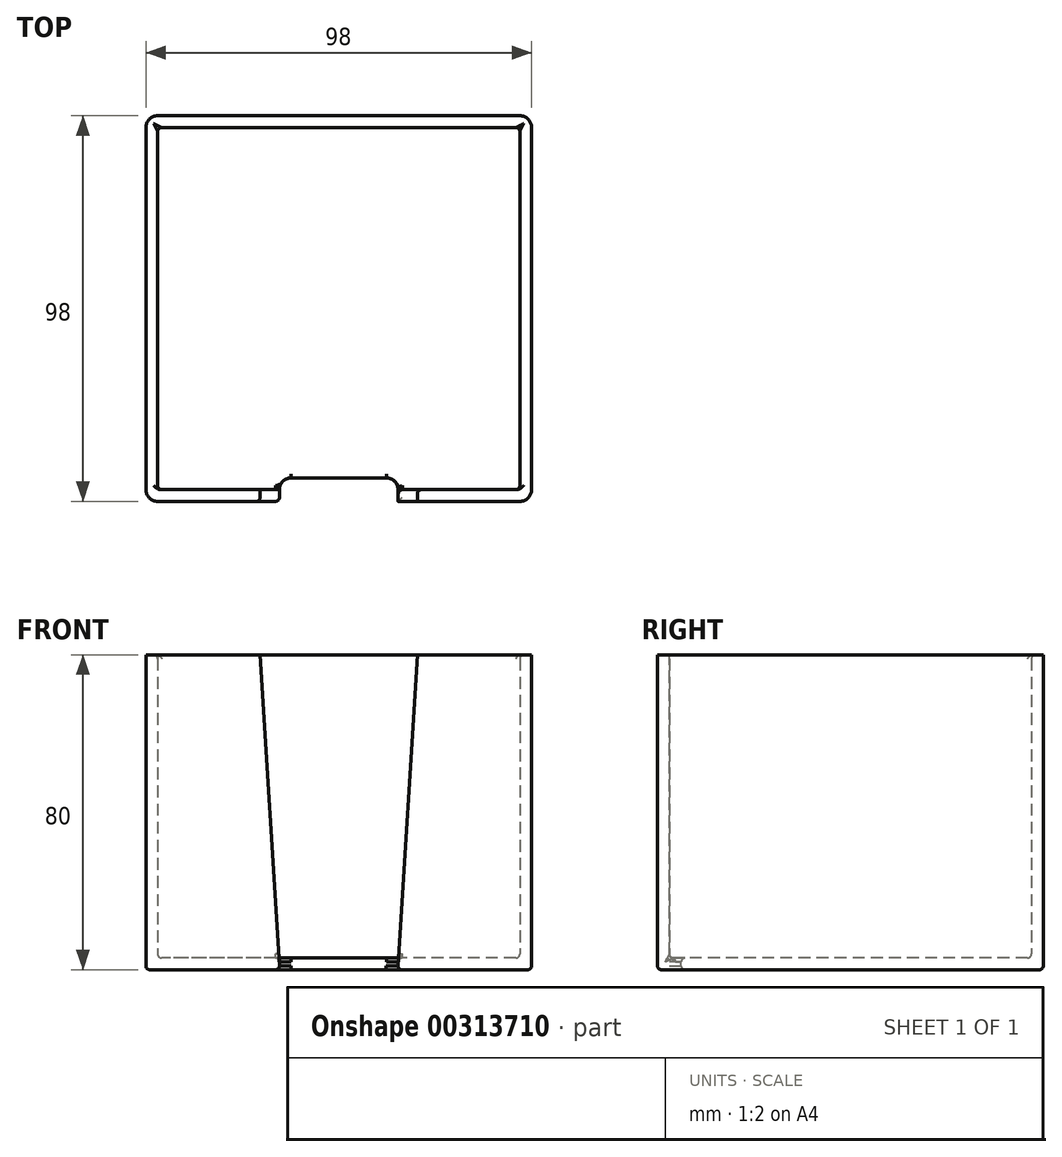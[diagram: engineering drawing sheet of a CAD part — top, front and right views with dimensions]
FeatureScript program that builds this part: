
annotation { "Feature Type Name" : "Feature", "Feature Type Description" : "" }
export const myFeature = defineFeature(function(context is Context, id is Id, definition is map)
    precondition{}
    {
        {
            var Q0;
            Q0=qCreatedBy(makeId("Top.planeOp"),FACE);
            var sketch = newSketch(context, id + "F0", { "sketchPlane" : qUnion([Q0])});
            skLineSegment(sketch, "E0.bottom", {"start": v(49, 49) * mm, "end": v(-49, 49) * mm});
            skLineSegment(sketch, "E0.top", {"start": v(49, -49) * mm, "end": v(-49, -49) * mm});
            skLineSegment(sketch, "E0.left", {"start": v(49, 49) * mm, "end": v(49, -49) * mm});
            skLineSegment(sketch, "E0.right", {"start": v(-49, 49) * mm, "end": v(-49, -49) * mm});
            skPoint(sketch, "E0.middle", {"position": v(0, 0) * mm});
            skSolve(sketch);
        }
        {
            var Q0;
            Q0 = qSketchRegion(id + "F0", true);
            extrude(context, id + "F1", {"entities" : qUnion([Q0]), "depth" : 80 * mm});
        }
        {
            var Q0;
            Q0=makeQuery(id+"F1.opExtrude","CAP_FACE",FACE,{"disambiguationData":[OSD([sQuery(id+"F0.wireOp",EDGE,"E0.bottom"),sQuery(id+"F0.wireOp",EDGE,"E0.top"),sQuery(id+"F0.wireOp",EDGE,"E0.left"),sQuery(id+"F0.wireOp",EDGE,"E0.right")])],"isStart":false});
            shell(context, id + "F2", {"entities" : qUnion([Q0]), "thickness" : 3 * mm});
        }
        {
            var Q0;
            Q0=makeQuery(id+"F1.opExtrude","SWEPT_FACE",FACE,{"disambiguationData":[OSD([sQuery(id+"F0.wireOp",EDGE,"E0.top")])]});
            var sketch = newSketch(context, id + "F3", { "sketchPlane" : qUnion([Q0])});
            skLineSegment(sketch, "E1", {"start": v(15, 0) * mm, "end": v(20, 80) * mm});
            skLineSegment(sketch, "E2.MirrorCS", {"start": v(-15, 0) * mm, "end": v(-20, 80) * mm});
            skLineSegment(sketch, "E3", {"start": v(-15, 0) * mm, "end": v(15, 0) * mm});
            skLineSegment(sketch, "E4", {"start": v(-20, 80) * mm, "end": v(20, 80) * mm});
            skSolve(sketch);
        }
        {
            var Q0;
            Q0=makeQuery(id+"F3.imprint","IMPRINT",FACE,{"disambiguationData":[TD([[makeQuery(id+"F3.imprint","IMPRINT",EDGE,{"derivedFrom":sQuery(id+"F3.wireOp",EDGE,"E1")}),1.0]])]});
            extrude(context, id + "F4", {"entities" : qUnion([Q0]), "operationType" : NewBodyOperationType.REMOVE, "oppositeDirection" : true, "depth" : 6 * mm});
        }
        {
            var Q0;
            Q0=makeQuery(id+"F1.opExtrude","SWEPT_EDGE",EDGE,{"disambiguationData":[OSD([sQuery(id+"F0.wireOp",EDGE,"E0.top"),sQuery(id+"F0.wireOp",EDGE,"E0.left")])]});
            var Q1;
            Q1=makeQuery(id+"F1.opExtrude","SWEPT_EDGE",EDGE,{"disambiguationData":[OSD([sQuery(id+"F0.wireOp",EDGE,"E0.top"),sQuery(id+"F0.wireOp",EDGE,"E0.right")])]});
            var Q2;
            Q2=makeQuery(id+"F1.opExtrude","SWEPT_EDGE",EDGE,{"disambiguationData":[OSD([sQuery(id+"F0.wireOp",EDGE,"E0.bottom"),sQuery(id+"F0.wireOp",EDGE,"E0.right")])]});
            var Q3;
            Q3=makeQuery(id+"F1.opExtrude","SWEPT_EDGE",EDGE,{"disambiguationData":[OSD([sQuery(id+"F0.wireOp",EDGE,"E0.bottom"),sQuery(id+"F0.wireOp",EDGE,"E0.left")])]});
            var Q4;
            Q4=makeQuery(id+"F4.boolean.opBoolean","COPY",EDGE,{"derivedFrom":makeQuery(id+"F4.opExtrude","CAP_EDGE",EDGE,{"disambiguationData":[OSD([sQuery(id+"F3.wireOp",EDGE,"E1")])],"isStart":false})});
            var Q5;
            Q5=makeQuery(id+"F4.boolean.opBoolean","COPY",EDGE,{"derivedFrom":makeQuery(id+"F4.opExtrude","CAP_EDGE",EDGE,{"disambiguationData":[OSD([sQuery(id+"F3.wireOp",EDGE,"E2.MirrorCS")])],"isStart":false})});
            var Q6;
            Q6=makeQuery(id+"F4.boolean.opBoolean","COPY",EDGE,{"derivedFrom":makeQuery(id+"F4.opExtrude","SWEPT_EDGE",EDGE,{"disambiguationData":[OSD([sQuery(id+"F0.wireOp",EDGE,"E0.top"),sQuery(id+"F3.wireOp",EDGE,"E2.MirrorCS"),sQuery(id+"F3.wireOp",EDGE,"E4")])]})});
            var Q7;
            Q7=makeQuery(id+"F4.boolean.opBoolean","COPY",EDGE,{"derivedFrom":makeQuery(id+"F4.opExtrude","SWEPT_EDGE",EDGE,{"disambiguationData":[OSD([sQuery(id+"F0.wireOp",EDGE,"E0.top"),sQuery(id+"F3.wireOp",EDGE,"E1"),sQuery(id+"F3.wireOp",EDGE,"E4")])]})});
            fillet(context, id + "F5", {"entities" : qUnion([Q0, Q1, Q2, Q3, Q4, Q5, Q6, Q7]), "radius" : 3 * mm, "tangentPropagation" : true, "allowEdgeOverflow" : false});
        }
        {
            var Q0;
            Q0=makeQuery(id+"F5.opFillet","BLEND_EDGE",EDGE,{"blendedFrom":[makeQuery(id+"F4.boolean.opBoolean","COPY",EDGE,{"derivedFrom":makeQuery(id+"F4.opExtrude","CAP_EDGE",EDGE,{"disambiguationData":[OSD([sQuery(id+"F3.wireOp",EDGE,"E2.MirrorCS")])],"isStart":false})}),makeQuery(id+"F2.opShell","OFFSET_FACE",FACE,{"disambiguationData":[OSD([sQuery(id+"F0.wireOp",EDGE,"E0.bottom"),sQuery(id+"F0.wireOp",EDGE,"E0.top"),sQuery(id+"F0.wireOp",EDGE,"E0.left"),sQuery(id+"F0.wireOp",EDGE,"E0.right")])]})],"blendedInto":[makeQuery(id+"F2.opShell","OFFSET_FACE",FACE,{"disambiguationData":[OSD([sQuery(id+"F0.wireOp",EDGE,"E0.bottom"),sQuery(id+"F0.wireOp",EDGE,"E0.top"),sQuery(id+"F0.wireOp",EDGE,"E0.left"),sQuery(id+"F0.wireOp",EDGE,"E0.right")])]})]});
            var Q1;
            Q1=makeQuery(id+"F4.boolean.opBoolean","INTERSECT",EDGE,{"derivedFrom":[makeQuery(id+"F2.opShell","OFFSET_FACE",FACE,{"disambiguationData":[OSD([sQuery(id+"F0.wireOp",EDGE,"E0.bottom"),sQuery(id+"F0.wireOp",EDGE,"E0.top"),sQuery(id+"F0.wireOp",EDGE,"E0.left"),sQuery(id+"F0.wireOp",EDGE,"E0.right")])]}),makeQuery(id+"F4.opExtrude","CAP_FACE",FACE,{"disambiguationData":[OSD([sQuery(id+"F3.wireOp",EDGE,"E1"),sQuery(id+"F3.wireOp",EDGE,"E2.MirrorCS"),sQuery(id+"F3.wireOp",EDGE,"E3"),sQuery(id+"F3.wireOp",EDGE,"E4")])],"isStart":false})]});
            var Q2;
            Q2=makeQuery(id+"F5.opFillet","BLEND_EDGE",EDGE,{"blendedFrom":[makeQuery(id+"F4.boolean.opBoolean","COPY",EDGE,{"derivedFrom":makeQuery(id+"F4.opExtrude","CAP_EDGE",EDGE,{"disambiguationData":[OSD([sQuery(id+"F3.wireOp",EDGE,"E1")])],"isStart":false})}),makeQuery(id+"F2.opShell","OFFSET_FACE",FACE,{"disambiguationData":[OSD([sQuery(id+"F0.wireOp",EDGE,"E0.bottom"),sQuery(id+"F0.wireOp",EDGE,"E0.top"),sQuery(id+"F0.wireOp",EDGE,"E0.left"),sQuery(id+"F0.wireOp",EDGE,"E0.right")])]})],"blendedInto":[makeQuery(id+"F2.opShell","OFFSET_FACE",FACE,{"disambiguationData":[OSD([sQuery(id+"F0.wireOp",EDGE,"E0.bottom"),sQuery(id+"F0.wireOp",EDGE,"E0.top"),sQuery(id+"F0.wireOp",EDGE,"E0.left"),sQuery(id+"F0.wireOp",EDGE,"E0.right")])]})]});
            var Q3;
            Q3=makeQuery(id+"F4.boolean.opBoolean","INTERSECT",EDGE,{"derivedFrom":[makeQuery(id+"F2.opShell","OFFSET_FACE",FACE,{"disambiguationData":[OSD([sQuery(id+"F0.wireOp",EDGE,"E0.top")])]}),makeQuery(id+"F4.opExtrude","SWEPT_FACE",FACE,{"disambiguationData":[OSD([sQuery(id+"F3.wireOp",EDGE,"E1")])]})]});
            var Q4;
            {var subQ0=sQuery(id+"F0.wireOp",EDGE,"E0.left");Q4=makeQuery(id+"F2.opShell","OFFSET_EDGE",EDGE,{"disambiguationData":[OSD([subQ0]),TDD([makeQuery(id+"F1.opExtrude","CAP_EDGE",EDGE,{"disambiguationData":[OSD([subQ0])],"isStart":false})])]});}
            var Q5;
            {var subQ0=sQuery(id+"F0.wireOp",EDGE,"E0.right");var subQ2=sQuery(id+"F0.wireOp",EDGE,"E0.top");var subQ4=sQuery(id+"F3.wireOp",EDGE,"E2.MirrorCS");Q5=makeQuery(id+"F5.opFillet","BLEND_EDGE",EDGE,{"blendedFrom":[makeQuery(id+"F4.boolean.opBoolean","COPY",EDGE,{"derivedFrom":makeQuery(id+"F4.opExtrude","SWEPT_EDGE",EDGE,{"disambiguationData":[OSD([subQ2,subQ4,sQuery(id+"F3.wireOp",EDGE,"E4")])]})}),makeQuery(id+"F4.boolean.opBoolean","SPLIT",FACE,{"disambiguationData":[TD([makeQuery(id+"F2.opShell","OFFSET_FACE",FACE,{"disambiguationData":[OSD([subQ0])]})])],"derivedFrom":makeQuery(id+"F2.opShell","OFFSET_FACE",FACE,{"disambiguationData":[OSD([subQ2])]})})],"blendedInto":[makeQuery(id+"F4.boolean.opBoolean","SPLIT",FACE,{"disambiguationData":[TD([makeQuery(id+"F2.opShell","OFFSET_FACE",FACE,{"disambiguationData":[OSD([subQ0])]})])],"derivedFrom":makeQuery(id+"F2.opShell","OFFSET_FACE",FACE,{"disambiguationData":[OSD([subQ2])]})})]});}
            var Q6;
            {var subQ0=sQuery(id+"F0.wireOp",EDGE,"E0.right");Q6=makeQuery(id+"F2.opShell","OFFSET_EDGE",EDGE,{"disambiguationData":[OSD([subQ0]),TDD([makeQuery(id+"F1.opExtrude","CAP_EDGE",EDGE,{"disambiguationData":[OSD([subQ0])],"isStart":false})])]});}
            var Q7;
            {var subQ0=sQuery(id+"F0.wireOp",EDGE,"E0.bottom");Q7=makeQuery(id+"F2.opShell","OFFSET_EDGE",EDGE,{"disambiguationData":[OSD([subQ0]),TDD([makeQuery(id+"F1.opExtrude","CAP_EDGE",EDGE,{"disambiguationData":[OSD([subQ0])],"isStart":false})])]});}
            var Q8;
            Q8=makeQuery(id+"F4.boolean.opBoolean","COPY",EDGE,{"derivedFrom":makeQuery(id+"F4.opExtrude","CAP_EDGE",EDGE,{"disambiguationData":[OSD([sQuery(id+"F3.wireOp",EDGE,"E2.MirrorCS")])],"isStart":true})});
            var Q9;
            {var subQ0=sQuery(id+"F0.wireOp",EDGE,"E0.right");var subQ2=sQuery(id+"F0.wireOp",EDGE,"E0.top");var subQ4=sQuery(id+"F3.wireOp",EDGE,"E2.MirrorCS");Q9=makeQuery(id+"F5.opFillet","BLEND_EDGE",EDGE,{"blendedFrom":[makeQuery(id+"F4.boolean.opBoolean","COPY",EDGE,{"derivedFrom":makeQuery(id+"F4.opExtrude","SWEPT_EDGE",EDGE,{"disambiguationData":[OSD([subQ2,subQ4,sQuery(id+"F3.wireOp",EDGE,"E4")])]})}),makeQuery(id+"F4.boolean.opBoolean","SPLIT",FACE,{"disambiguationData":[TD([makeQuery(id+"F1.opExtrude","SWEPT_FACE",FACE,{"disambiguationData":[OSD([subQ0])]})])],"derivedFrom":makeQuery(id+"F1.opExtrude","SWEPT_FACE",FACE,{"disambiguationData":[OSD([subQ2])]})})],"blendedInto":[makeQuery(id+"F4.boolean.opBoolean","SPLIT",FACE,{"disambiguationData":[TD([makeQuery(id+"F1.opExtrude","SWEPT_FACE",FACE,{"disambiguationData":[OSD([subQ0])]})])],"derivedFrom":makeQuery(id+"F1.opExtrude","SWEPT_FACE",FACE,{"disambiguationData":[OSD([subQ2])]})})]});}
            var Q10;
            Q10=makeQuery(id+"F1.opExtrude","CAP_FACE",FACE,{"disambiguationData":[OSD([sQuery(id+"F0.wireOp",EDGE,"E0.bottom"),sQuery(id+"F0.wireOp",EDGE,"E0.top"),sQuery(id+"F0.wireOp",EDGE,"E0.left"),sQuery(id+"F0.wireOp",EDGE,"E0.right")])],"isStart":true});
            fillet(context, id + "F6", {"entities" : qUnion([Q0, Q1, Q2, Q3, Q4, Q5, Q6, Q7, Q8, Q9, Q10]), "radius" : 1 * mm, "tangentPropagation" : true, "allowEdgeOverflow" : false});
        }
        {
            var Q0;
            Q0=makeQuery(id+"F2.opShell","OFFSET_EDGE",EDGE,{"disambiguationData":[OSD([sQuery(id+"F0.wireOp",EDGE,"E0.bottom"),sQuery(id+"F0.wireOp",EDGE,"E0.left")])]});
            var Q1;
            Q1=makeQuery(id+"F2.opShell","OFFSET_EDGE",EDGE,{"disambiguationData":[OSD([sQuery(id+"F0.wireOp",EDGE,"E0.top"),sQuery(id+"F0.wireOp",EDGE,"E0.left")])]});
            var Q2;
            Q2=makeQuery(id+"F2.opShell","OFFSET_EDGE",EDGE,{"disambiguationData":[OSD([sQuery(id+"F0.wireOp",EDGE,"E0.top"),sQuery(id+"F0.wireOp",EDGE,"E0.right")])]});
            var Q3;
            Q3=makeQuery(id+"F2.opShell","OFFSET_EDGE",EDGE,{"disambiguationData":[OSD([sQuery(id+"F0.wireOp",EDGE,"E0.bottom"),sQuery(id+"F0.wireOp",EDGE,"E0.right")])]});
            var Q4;
            {var subQ0=sQuery(id+"F0.wireOp",EDGE,"E0.left");Q4=makeQuery(id+"F2.opShell","OFFSET_EDGE",EDGE,{"disambiguationData":[OSD([subQ0]),TDD([makeQuery(id+"F1.opExtrude","CAP_EDGE",EDGE,{"disambiguationData":[OSD([subQ0])],"isStart":true})])]});}
            var Q5;
            Q5=makeQuery(id+"F2.opShell","OFFSET_FACE",FACE,{"disambiguationData":[OSD([sQuery(id+"F0.wireOp",EDGE,"E0.bottom"),sQuery(id+"F0.wireOp",EDGE,"E0.top"),sQuery(id+"F0.wireOp",EDGE,"E0.left"),sQuery(id+"F0.wireOp",EDGE,"E0.right")])]});
            fillet(context, id + "F7", {"entities" : qUnion([Q0, Q1, Q2, Q3, Q4, Q5]), "radius" : 1 * mm, "tangentPropagation" : true, "allowEdgeOverflow" : false});
        }
    });
